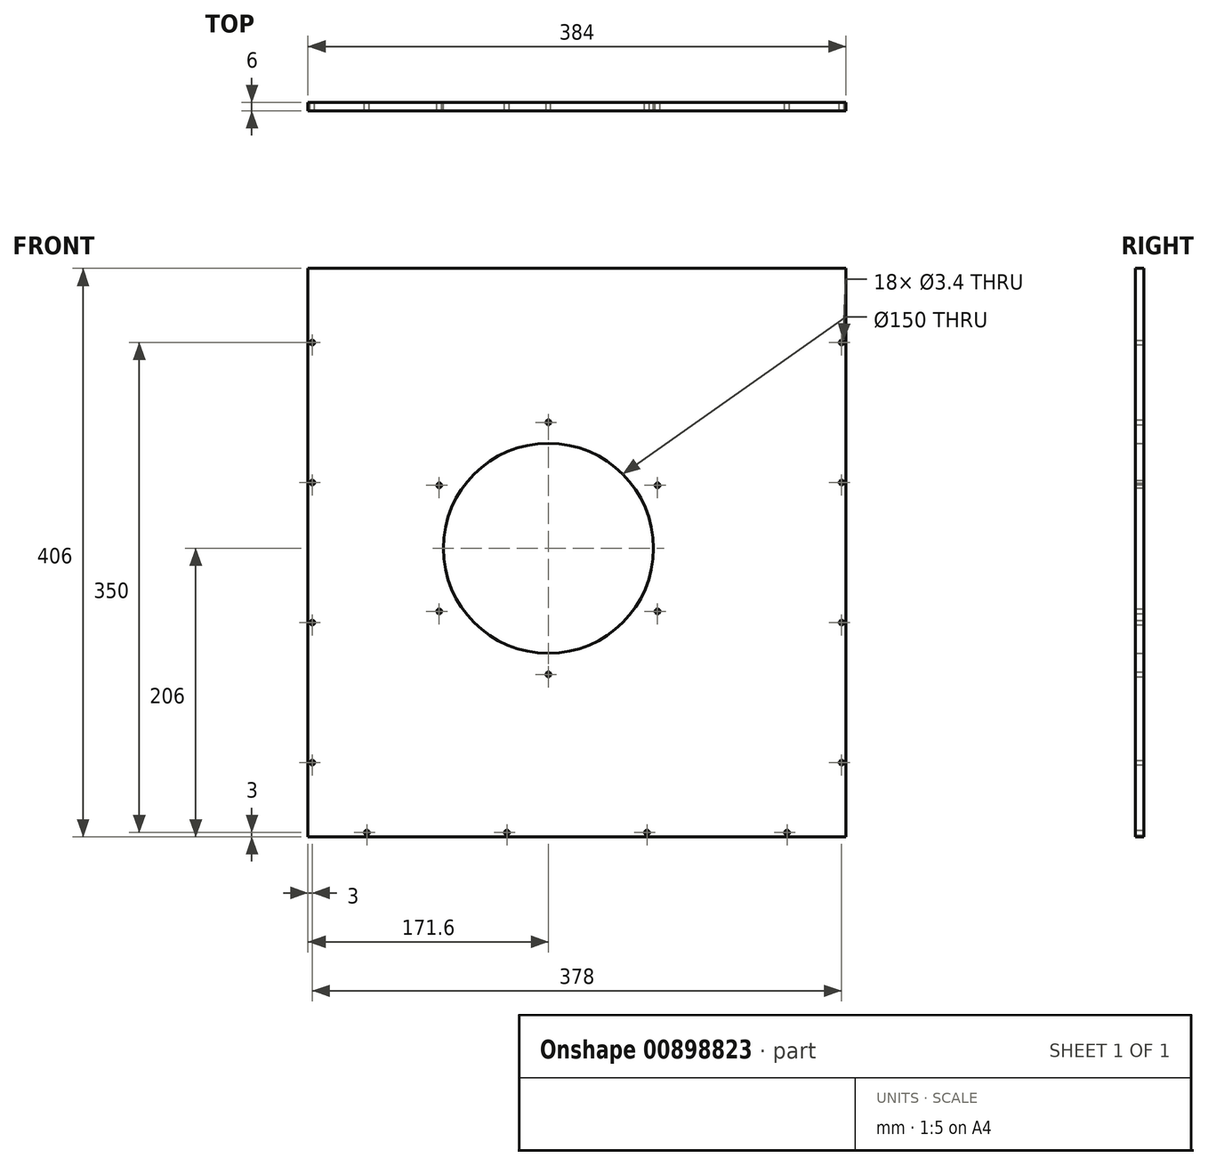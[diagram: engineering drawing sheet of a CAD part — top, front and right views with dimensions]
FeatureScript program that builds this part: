
annotation { "Feature Type Name" : "Feature", "Feature Type Description" : "" }
export const myFeature = defineFeature(function(context is Context, id is Id, definition is map)
    precondition{}
    {
        {
            var Q0;
            Q0=qCreatedBy(makeId("Front.planeOp"),FACE);
            var sketch = newSketch(context, id + "F0", { "sketchPlane" : qUnion([Q0])});
            skLineSegment(sketch, "E0.bottom", {"start": v(-192, 203) * mm, "end": v(192, 203) * mm});
            skLineSegment(sketch, "E0.top", {"start": v(-192, -203) * mm, "end": v(192, -203) * mm});
            skLineSegment(sketch, "E0.left", {"start": v(-192, 203) * mm, "end": v(-192, -203) * mm});
            skLineSegment(sketch, "E0.right", {"start": v(192, 203) * mm, "end": v(192, -203) * mm});
            skPoint(sketch, "E0.middle", {"position": v(0, 0) * mm});
            skSolve(sketch);
        }
        {
            var Q0;
            Q0=makeQuery(id+"F0.imprint","IMPRINT",FACE,{"disambiguationData":[TD([[makeQuery(id+"F0.imprint","IMPRINT",EDGE,{"derivedFrom":sQuery(id+"F0.wireOp",EDGE,"E0.bottom")}),-1.0]])]});
            var sketch = newSketch(context, id + "F1", { "sketchPlane" : qUnion([Q0])});
            skPoint(sketch, "E1", {"position": v(150, -200) * mm});
            skPoint(sketch, "E2", {"position": v(-50, -200) * mm});
            skPoint(sketch, "E3", {"position": v(-150, -200) * mm});
            skPoint(sketch, "E4", {"position": v(-189, 50) * mm});
            skPoint(sketch, "E5", {"position": v(-189, 150) * mm});
            skPoint(sketch, "E6", {"position": v(189, -150) * mm});
            skPoint(sketch, "E7", {"position": v(189, 50) * mm});
            skPoint(sketch, "E8", {"position": v(189, 150) * mm});
            skPoint(sketch, "E9", {"position": v(-189, -50) * mm});
            skPoint(sketch, "E10", {"position": v(189, -50) * mm});
            skPoint(sketch, "E11", {"position": v(-189, -150) * mm});
            skPoint(sketch, "E12", {"position": v(50, -200) * mm});
            skSolve(sketch);
        }
        {
            var Q0;
            Q0 = qSketchRegion(id + "F0", true);
            extrude(context, id + "F2", {"entities" : qUnion([Q0]), "depth" : 6 * mm, "offsetDistance" : 25 * mm});
        }
        {
            var Q0;
            Q0=sQuery(id+"F1.wireOp",VERTEX,"E8");
            var Q1;
            Q1=sQuery(id+"F1.wireOp",VERTEX,"E7");
            var Q2;
            Q2=sQuery(id+"F1.wireOp",VERTEX,"E6");
            var Q3;
            Q3=sQuery(id+"F1.wireOp",VERTEX,"E1");
            var Q4;
            Q4=sQuery(id+"F1.wireOp",VERTEX,"E2");
            var Q5;
            Q5=sQuery(id+"F1.wireOp",VERTEX,"E3");
            var Q6;
            Q6=sQuery(id+"F1.wireOp",VERTEX,"0d7333b4-9ded-4a55-a868-df6adb02dbac");
            var Q7;
            Q7=sQuery(id+"F1.wireOp",VERTEX,"E4");
            var Q8;
            Q8=sQuery(id+"F1.wireOp",VERTEX,"E5");
            var Q9;
            Q9=sQuery(id+"F1.wireOp",VERTEX,"E9");
            var Q10;
            Q10=sQuery(id+"F1.wireOp",VERTEX,"1628c584-3f5b-4b04-a3a9-7816295e86bf");
            var Q11;
            Q11=sQuery(id+"F1.wireOp",VERTEX,"b0da5489-ae61-4902-be5b-5bf197866a6a");
            var Q12;
            Q12=makeQuery(id+"F2.opExtrude","SWEPT_BODY",BODY,{"disambiguationData":[OSD([sQuery(id+"F0.wireOp",EDGE,"E0.bottom"),sQuery(id+"F0.wireOp",EDGE,"E0.top"),sQuery(id+"F0.wireOp",EDGE,"E0.left"),sQuery(id+"F0.wireOp",EDGE,"E0.right")])]});
            hole(context, id + "F3", {"style" : HoleStyle.SIMPLE, "endStyle" : HoleEndStyle.THROUGH, "oppositeDirection" : true, "standardTappedOrClearance" : lookupTablePath({ "fit" : "Normal", "standard" : "ISO", "size" : "M3", "type" : "Clearance" }), "standardBlindInLast" : lookupTablePath({ "fit" : "Normal", "standard" : "ISO", "size" : "M3", "type" : "Clearance" }), "holeDiameter" : 3.4 * mm, "majorDiameter" : 5 * mm, "tappedDepth" : 15 * mm, "tapClearance" : 3, "locations" : qUnion([Q0, Q1, Q2, Q3, Q4, Q5, Q6, Q7, Q8, Q9, Q10, Q11]), "scope" : qUnion([Q12])});
        }
        {
            var Q0;
            Q0=makeQuery(id+"F2.opExtrude","CAP_FACE",FACE,{"disambiguationData":[OSD([sQuery(id+"F0.wireOp",EDGE,"E0.bottom"),sQuery(id+"F0.wireOp",EDGE,"E0.top"),sQuery(id+"F0.wireOp",EDGE,"E0.left"),sQuery(id+"F0.wireOp",EDGE,"E0.right")])],"isStart":true});
            var sketch = newSketch(context, id + "F4", { "sketchPlane" : qUnion([Q0])});
            skPoint(sketch, "E13", {"position": v(122, -203) * mm});
            skPoint(sketch, "E14", {"position": v(122, 3) * mm});
            skLineSegment(sketch, "E15", {"start": v(122, -203) * mm, "end": v(122, 3) * mm, "construction": true});
            skLineSegment(sketch, "E16", {"start": v(122, 3) * mm, "end": v(192, 3) * mm, "construction": true});
            skPoint(sketch, "E17", {"position": v(20.4, 3) * mm});
            skCircle(sketch, "E18", {"center": v(20.4, 3) * mm, "radius": 75 * mm});
            skCircle(sketch, "E19", {"center": v(20.4, 3) * mm, "radius": 90 * mm, "construction": true});
            skPoint(sketch, "E20", {"position": v(98.34, 48) * mm});
            skPoint(sketch, "E21", {"position": v(-57.54, 48) * mm});
            skPoint(sketch, "E22", {"position": v(20.4, -87) * mm});
            skLineSegment(sketch, "E23", {"start": v(20.4, -87) * mm, "end": v(20.4, 3) * mm, "construction": true});
            skLineSegment(sketch, "E24", {"start": v(98.34, 48) * mm, "end": v(20.4, 3) * mm, "construction": true});
            skLineSegment(sketch, "E25", {"start": v(20.4, 3) * mm, "end": v(-57.54, 48) * mm, "construction": true});
            skPoint(sketch, "E26", {"position": v(98.34, -42) * mm});
            skPoint(sketch, "E27", {"position": v(20.4, 93) * mm});
            skPoint(sketch, "E28", {"position": v(-57.54, -42) * mm});
            skLineSegment(sketch, "E29", {"start": v(98.34, -42) * mm, "end": v(20.4, 3) * mm, "construction": true});
            skLineSegment(sketch, "E30", {"start": v(20.4, 3) * mm, "end": v(-57.54, -42) * mm, "construction": true});
            skLineSegment(sketch, "E31", {"start": v(20.4, 3) * mm, "end": v(20.4, 93) * mm, "construction": true});
            skSolve(sketch);
        }
        {
            var Q0;
            Q0=sQuery(id+"F4.wireOp",VERTEX,"E20");
            var Q1;
            Q1=sQuery(id+"F4.wireOp",VERTEX,"E22");
            var Q2;
            Q2=sQuery(id+"F4.wireOp",VERTEX,"E21");
            var Q3;
            Q3=sQuery(id+"F4.wireOp",VERTEX,"E26");
            var Q4;
            Q4=sQuery(id+"F4.wireOp",VERTEX,"E27");
            var Q5;
            Q5=sQuery(id+"F4.wireOp",VERTEX,"E28");
            var Q6;
            Q6=makeQuery(id+"F2.opExtrude","SWEPT_BODY",BODY,{"disambiguationData":[OSD([sQuery(id+"F0.wireOp",EDGE,"E0.bottom"),sQuery(id+"F0.wireOp",EDGE,"E0.top"),sQuery(id+"F0.wireOp",EDGE,"E0.left"),sQuery(id+"F0.wireOp",EDGE,"E0.right")])]});
            hole(context, id + "F5", {"style" : HoleStyle.SIMPLE, "endStyle" : HoleEndStyle.THROUGH, "standardTappedOrClearance" : lookupTablePath({ "fit" : "Normal", "standard" : "ISO", "size" : "M3", "type" : "Clearance" }), "standardBlindInLast" : lookupTablePath({ "fit" : "Normal", "standard" : "ISO", "size" : "M3", "type" : "Clearance" }), "holeDiameter" : 3.4 * mm, "majorDiameter" : 3 * mm, "tappedDepth" : 15 * mm, "tapClearance" : 3, "locations" : qUnion([Q0, Q1, Q2, Q3, Q4, Q5]), "scope" : qUnion([Q6])});
        }
        {
            var Q0;
            Q0 = qSketchRegion(id + "F4", true);
            extrude(context, id + "F6", {"entities" : qUnion([Q0]), "oppositeDirection" : true, "depth" : 6 * mm, "offsetDistance" : 25 * mm});
        }
        {
            var Q0;
            Q0=makeQuery(id+"F6.opExtrude","SWEPT_BODY",BODY,{"disambiguationData":[OSD([sQuery(id+"F4.wireOp",EDGE,"E18")])]});
            var Q1;
            Q1=makeQuery(id+"F2.opExtrude","SWEPT_BODY",BODY,{"disambiguationData":[OSD([sQuery(id+"F0.wireOp",EDGE,"E0.bottom"),sQuery(id+"F0.wireOp",EDGE,"E0.top"),sQuery(id+"F0.wireOp",EDGE,"E0.left"),sQuery(id+"F0.wireOp",EDGE,"E0.right")])]});
            booleanBodies(context, id + "F7", {"operationType" : BooleanOperationType.SUBTRACTION, "tools" : qUnion([Q0]), "targets" : qUnion([Q1])});
        }
        {
            var Q0;
            Q0=sQuery(id+"F1.wireOp",VERTEX,"E11");
            var Q1;
            Q1=makeQuery(id+"F2.opExtrude","SWEPT_BODY",BODY,{"disambiguationData":[OSD([sQuery(id+"F0.wireOp",EDGE,"E0.bottom"),sQuery(id+"F0.wireOp",EDGE,"E0.top"),sQuery(id+"F0.wireOp",EDGE,"E0.left"),sQuery(id+"F0.wireOp",EDGE,"E0.right")])]});
            hole(context, id + "F8", {"style" : HoleStyle.SIMPLE, "endStyle" : HoleEndStyle.THROUGH, "oppositeDirection" : true, "standardTappedOrClearance" : lookupTablePath({ "fit" : "Normal", "standard" : "ISO", "size" : "M3", "type" : "Clearance" }), "standardBlindInLast" : lookupTablePath({ "fit" : "Normal", "standard" : "ISO", "engagement" : "75%", "pitch" : "0.5 mm", "size" : "M3", "type" : "Clearance & tapped" }), "holeDiameter" : 3.4 * mm, "majorDiameter" : 5 * mm, "tappedDepth" : 15 * mm, "tapClearance" : 3, "locations" : qUnion([Q0]), "scope" : qUnion([Q1])});
        }
        {
            var Q0;
            Q0=sQuery(id+"F1.wireOp",VERTEX,"E10");
            var Q1;
            Q1=makeQuery(id+"F2.opExtrude","SWEPT_BODY",BODY,{"disambiguationData":[OSD([sQuery(id+"F0.wireOp",EDGE,"E0.bottom"),sQuery(id+"F0.wireOp",EDGE,"E0.top"),sQuery(id+"F0.wireOp",EDGE,"E0.left"),sQuery(id+"F0.wireOp",EDGE,"E0.right")])]});
            hole(context, id + "F9", {"style" : HoleStyle.SIMPLE, "endStyle" : HoleEndStyle.THROUGH, "oppositeDirection" : true, "standardTappedOrClearance" : lookupTablePath({ "fit" : "Normal", "standard" : "ISO", "size" : "M3", "type" : "Clearance" }), "standardBlindInLast" : lookupTablePath({ "fit" : "Normal", "standard" : "ISO", "engagement" : "75%", "pitch" : "0.5 mm", "size" : "M3", "type" : "Clearance & tapped" }), "holeDiameter" : 3.4 * mm, "majorDiameter" : 5 * mm, "tappedDepth" : 15 * mm, "tapClearance" : 3, "locations" : qUnion([Q0]), "scope" : qUnion([Q1])});
        }
        {
            var Q0;
            Q0=sQuery(id+"F1.wireOp",VERTEX,"E12");
            var Q1;
            Q1=makeQuery(id+"F2.opExtrude","SWEPT_BODY",BODY,{"disambiguationData":[OSD([sQuery(id+"F0.wireOp",EDGE,"E0.bottom"),sQuery(id+"F0.wireOp",EDGE,"E0.top"),sQuery(id+"F0.wireOp",EDGE,"E0.left"),sQuery(id+"F0.wireOp",EDGE,"E0.right")])]});
            hole(context, id + "F10", {"style" : HoleStyle.SIMPLE, "endStyle" : HoleEndStyle.THROUGH, "oppositeDirection" : true, "standardTappedOrClearance" : lookupTablePath({ "fit" : "Normal", "standard" : "ISO", "size" : "M3", "type" : "Clearance" }), "standardBlindInLast" : lookupTablePath({ "fit" : "Normal", "standard" : "ISO", "engagement" : "75%", "pitch" : "0.5 mm", "size" : "M3", "type" : "Clearance & tapped" }), "holeDiameter" : 3.4 * mm, "majorDiameter" : 5 * mm, "tappedDepth" : 15 * mm, "tapClearance" : 3, "locations" : qUnion([Q0]), "scope" : qUnion([Q1])});
        }
    });
